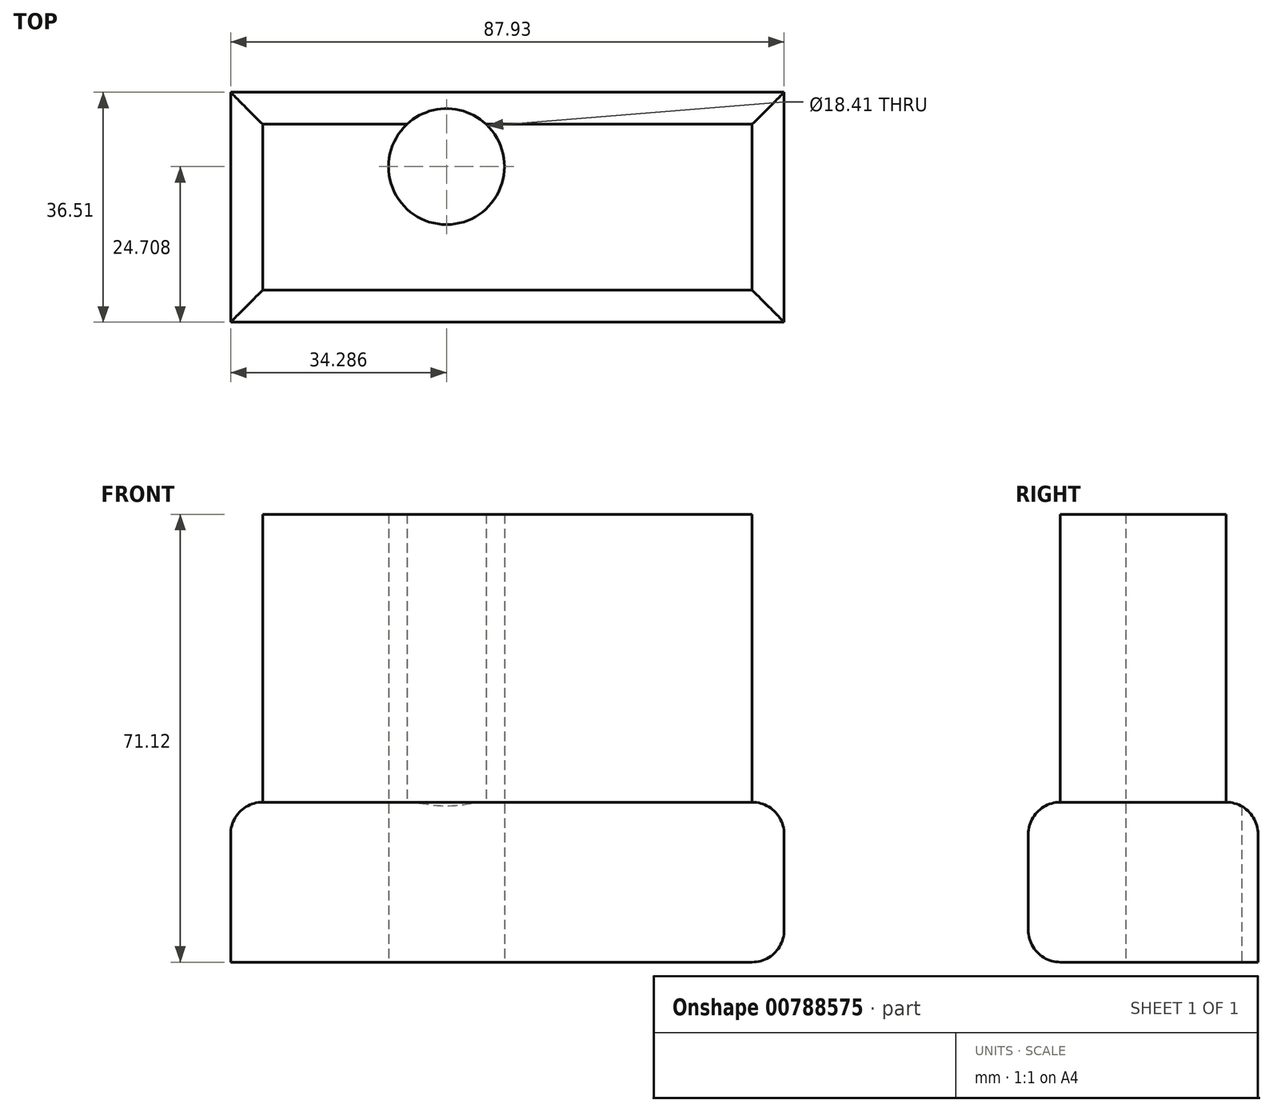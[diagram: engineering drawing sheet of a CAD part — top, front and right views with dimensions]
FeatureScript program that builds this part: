
annotation { "Feature Type Name" : "Feature", "Feature Type Description" : "" }
export const myFeature = defineFeature(function(context is Context, id is Id, definition is map)
    precondition{}
    {
        {
            var Q0;
            Q0=qCreatedBy(makeId("Top.planeOp"),FACE);
            var sketch = newSketch(context, id + "F0", { "sketchPlane" : qUnion([Q0])});
            skLineSegment(sketch, "E0.bottom", {"start": v(-45.44, 15.95) * mm, "end": v(42.5, 15.95) * mm});
            skLineSegment(sketch, "E0.top", {"start": v(-45.44, -20.56) * mm, "end": v(42.5, -20.56) * mm});
            skLineSegment(sketch, "E0.left", {"start": v(-45.44, 15.95) * mm, "end": v(-45.44, -20.56) * mm});
            skLineSegment(sketch, "E0.right", {"start": v(42.5, 15.95) * mm, "end": v(42.5, -20.56) * mm});
            skCircle(sketch, "E1", {"center": v(-11.15, 4.15) * mm, "radius": 9.2 * mm});
            skSolve(sketch);
        }
        {
            var Q0;
            Q0 = qSketchRegion(id + "F0", true);
            extrude(context, id + "F1", {"entities" : qUnion([Q0]), "depth" : 25.4 * mm, "offsetDistance" : 25.4 * mm});
        }
        {
            var Q0;
            Q0=makeQuery(id+"F1.opExtrude","CAP_EDGE",EDGE,{"disambiguationData":[OSD([sQuery(id+"F0.wireOp",EDGE,"E0.top")])],"isStart":false});
            var Q1;
            Q1=makeQuery(id+"F1.opExtrude","CAP_EDGE",EDGE,{"disambiguationData":[OSD([sQuery(id+"F0.wireOp",EDGE,"E0.bottom")])],"isStart":false});
            var Q2;
            Q2=makeQuery(id+"F1.opExtrude","CAP_EDGE",EDGE,{"disambiguationData":[OSD([sQuery(id+"F0.wireOp",EDGE,"E0.left")])],"isStart":false});
            var Q3;
            Q3=makeQuery(id+"F1.opExtrude","CAP_EDGE",EDGE,{"disambiguationData":[OSD([sQuery(id+"F0.wireOp",EDGE,"E0.right")])],"isStart":false});
            var Q4;
            Q4=makeQuery(id+"F1.opExtrude","CAP_EDGE",EDGE,{"disambiguationData":[OSD([sQuery(id+"F0.wireOp",EDGE,"E0.right")])],"isStart":true});
            var Q5;
            Q5=makeQuery(id+"F1.opExtrude","CAP_EDGE",EDGE,{"disambiguationData":[OSD([sQuery(id+"F0.wireOp",EDGE,"E0.top")])],"isStart":true});
            fillet(context, id + "F2", {"entities" : qUnion([Q0, Q1, Q2, Q3, Q4, Q5]), "radius" : 5.08 * mm, "tangentPropagation" : true, "allowEdgeOverflow" : false});
        }
        {
            var Q0;
            Q0=makeQuery(id+"F1.opExtrude","CAP_FACE",FACE,{"disambiguationData":[OSD([sQuery(id+"F0.wireOp",EDGE,"E0.bottom"),sQuery(id+"F0.wireOp",EDGE,"E0.top"),sQuery(id+"F0.wireOp",EDGE,"E0.left"),sQuery(id+"F0.wireOp",EDGE,"E0.right"),sQuery(id+"F0.wireOp",EDGE,"E1")])],"isStart":false});
            extrude(context, id + "F3", {"entities" : qUnion([Q0]), "operationType" : NewBodyOperationType.ADD, "depth" : 45.72 * mm, "offsetDistance" : 25.4 * mm});
        }
    });
